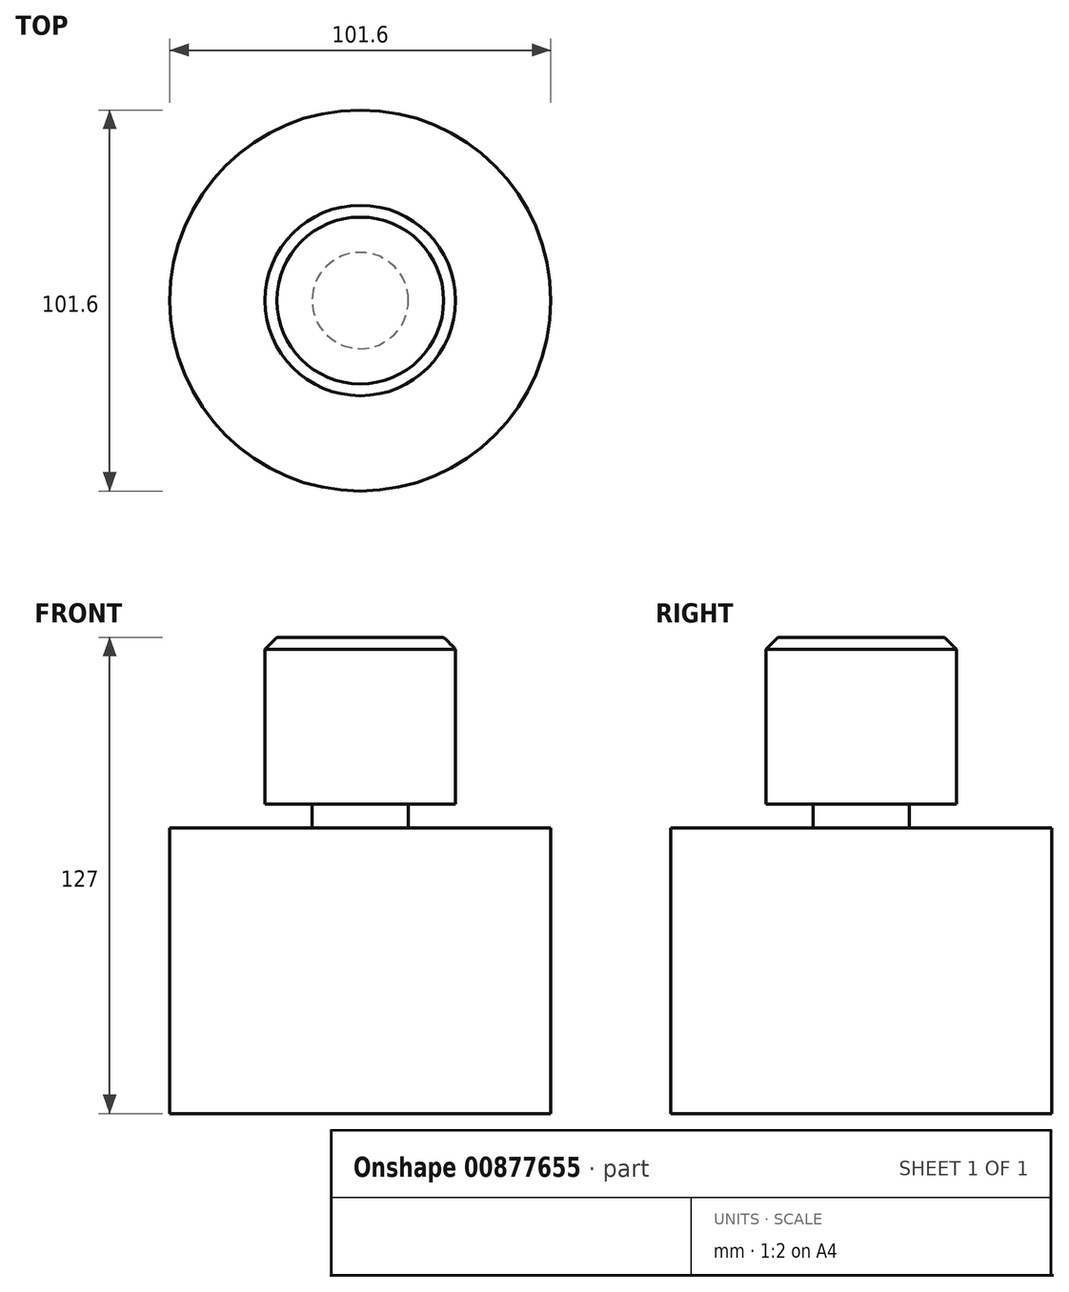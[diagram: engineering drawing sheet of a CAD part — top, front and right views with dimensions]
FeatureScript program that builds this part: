
annotation { "Feature Type Name" : "Feature", "Feature Type Description" : "" }
export const myFeature = defineFeature(function(context is Context, id is Id, definition is map)
    precondition{}
    {
        {
            var Q0;
            Q0=qCreatedBy(makeId("Top.planeOp"),FACE);
            var sketch = newSketch(context, id + "F0", { "sketchPlane" : qUnion([Q0])});
            skCircle(sketch, "E0", {"center": v(0, 0) * mm, "radius": 50.8 * mm});
            skSolve(sketch);
        }
        {
            var Q0;
            Q0 = qSketchRegion(id + "F0", true);
            extrude(context, id + "F1", {"entities" : qUnion([Q0]), "depth" : 76.2 * mm, "offsetDistance" : 25.4 * mm});
        }
        {
            var Q0;
            Q0=makeQuery(id+"F1.opExtrude","CAP_FACE",FACE,{"disambiguationData":[OSD([sQuery(id+"F0.wireOp",EDGE,"E0")])],"isStart":false});
            var sketch = newSketch(context, id + "F2", { "sketchPlane" : qUnion([Q0])});
            skCircle(sketch, "E1", {"center": v(0, 0) * mm, "radius": 12.83 * mm});
            skSolve(sketch);
        }
        {
            var Q0;
            Q0=makeQuery(id+"F2.imprint","IMPRINT",FACE,{"disambiguationData":[TD([[makeQuery(id+"F2.imprint","IMPRINT",EDGE,{"derivedFrom":sQuery(id+"F2.wireOp",EDGE,"E1")}),1.0]])]});
            extrude(context, id + "F3", {"entities" : qUnion([Q0]), "operationType" : NewBodyOperationType.ADD, "depth" : 6.35 * mm, "offsetDistance" : 25.4 * mm});
        }
        {
            var Q0;
            Q0=makeQuery(id+"F3.opExtrude","CAP_FACE",FACE,{"disambiguationData":[OSD([sQuery(id+"F2.wireOp",EDGE,"E1")])],"isStart":false});
            var sketch = newSketch(context, id + "F4", { "sketchPlane" : qUnion([Q0])});
            skCircle(sketch, "E2", {"center": v(0, 0) * mm, "radius": 25.4 * mm});
            skSolve(sketch);
        }
        {
            var Q0;
            Q0 = qSketchRegion(id + "F4", true);
            extrude(context, id + "F5", {"entities" : qUnion([Q0]), "operationType" : NewBodyOperationType.ADD, "depth" : 44.45 * mm, "offsetDistance" : 25.4 * mm});
        }
        {
            var Q0;
            Q0=makeQuery(id+"F5.opExtrude","CAP_FACE",FACE,{"disambiguationData":[OSD([sQuery(id+"F4.wireOp",EDGE,"E2")])],"isStart":false});
            chamfer(context, id + "F6", {"entities" : qUnion([Q0]), "width" : 3.17 * mm, "tangentPropagation" : true});
        }
    });
